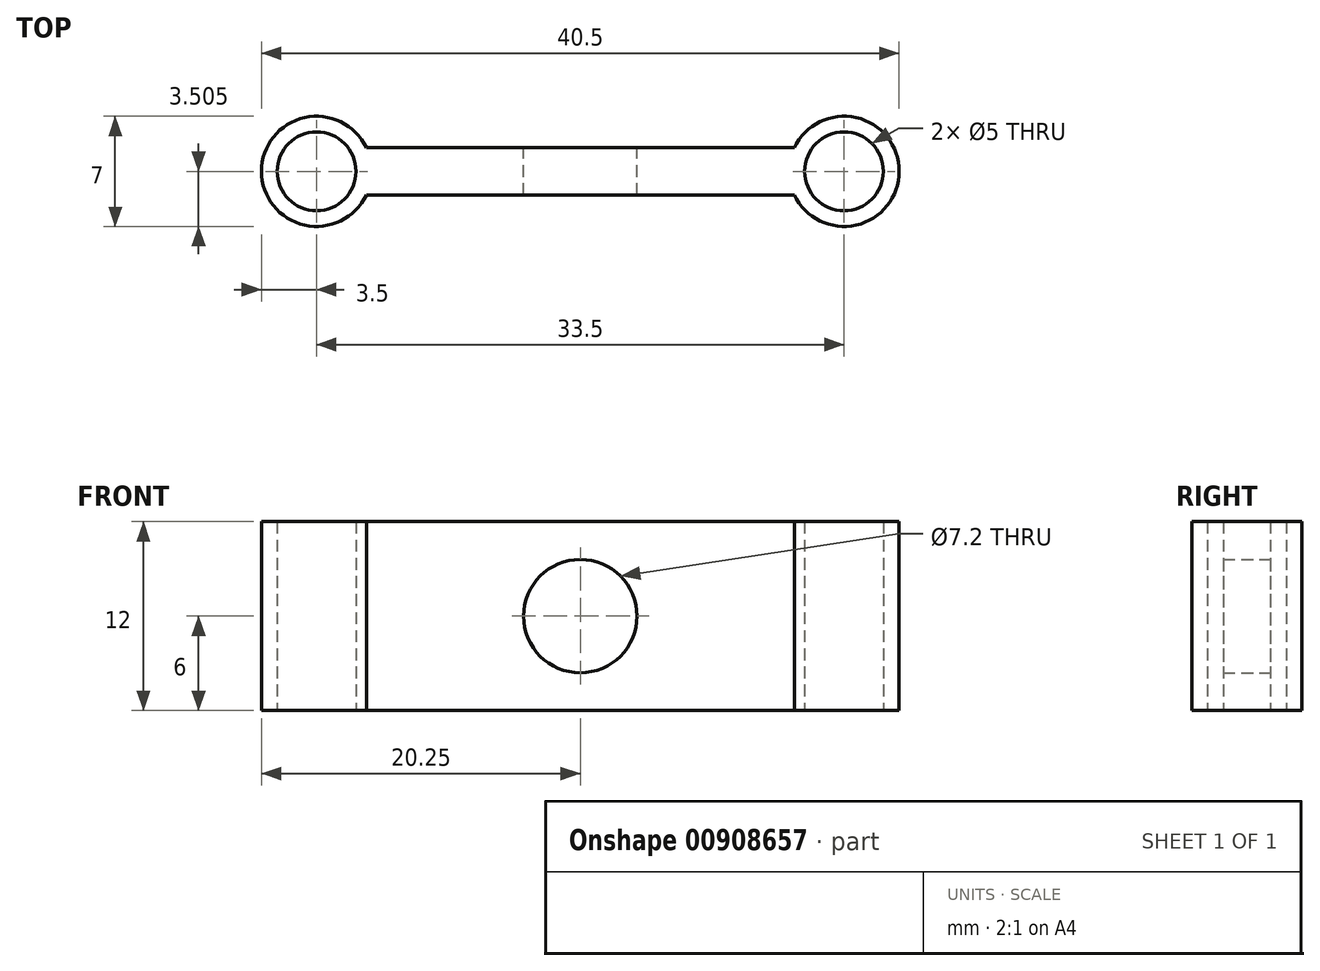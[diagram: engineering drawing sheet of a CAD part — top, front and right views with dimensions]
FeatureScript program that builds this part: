
annotation { "Feature Type Name" : "Feature", "Feature Type Description" : "" }
export const myFeature = defineFeature(function(context is Context, id is Id, definition is map)
    precondition{}
    {
        {
            var Q0;
            Q0=qCreatedBy(makeId("Top.planeOp"),FACE);
            var sketch = newSketch(context, id + "F0", { "sketchPlane" : qUnion([Q0])});
            skLineSegment(sketch, "E0.bottom", {"start": v(-14.5, 1.12) * mm, "end": v(19, 1.12) * mm});
            skLineSegment(sketch, "E0.top", {"start": v(-14.5, -1.88) * mm, "end": v(19, -1.88) * mm});
            skLineSegment(sketch, "E0.left", {"start": v(-14.5, 1.12) * mm, "end": v(-14.5, -1.88) * mm});
            skLineSegment(sketch, "E0.right", {"start": v(19, 1.12) * mm, "end": v(19, -1.88) * mm});
            skPoint(sketch, "E1", {"position": v(-14.5, -0.38) * mm});
            skCircle(sketch, "E2", {"center": v(-14.5, -0.38) * mm, "radius": 3.5 * mm});
            skCircle(sketch, "E3", {"center": v(19, -0.38) * mm, "radius": 3.5 * mm});
            skSolve(sketch);
        }
        {
            var Q0;
            Q0=qSketchRegion(id+"F0",true);
            extrude(context, id + "F1", {"entities" : qUnion([Q0]), "depth" : 12 * mm, "offsetDistance" : 25 * mm});
        }
        {
            var Q0;
            Q0=sQuery(id+"F0.wireOp",VERTEX,"35dba5de-8aa0-4c4d-8b60-120a7edc57c8");
            var Q1;
            Q1=sQuery(id+"F0.wireOp",VERTEX,"E3.center");
            var Q2;
            Q2=makeQuery(id+"F1.opExtrude","SWEPT_BODY",BODY,{"disambiguationData":[OSD([sQuery(id+"F0.wireOp",EDGE,"E0.bottom"),sQuery(id+"F0.wireOp",EDGE,"E0.top"),sQuery(id+"F0.wireOp",EDGE,"E2"),sQuery(id+"F0.wireOp",EDGE,"E3")])]});
            hole(context, id + "F2", {"style" : HoleStyle.SIMPLE, "endStyle" : HoleEndStyle.BLIND, "oppositeDirection" : true, "holeDiameter" : 5 * mm, "majorDiameter" : 5 * mm, "holeDepth" : 15 * mm, "isTappedThrough" : true, "tappedDepth" : 12 * mm, "tapClearance" : 3, "locations" : qUnion([Q0, Q1]), "scope" : qUnion([Q2])});
        }
        {
            var Q0;
            Q0=sQuery(id+"F0.wireOp",VERTEX,"E1");
            var Q1;
            Q1=makeQuery(id+"F1.opExtrude","SWEPT_BODY",BODY,{"disambiguationData":[OSD([sQuery(id+"F0.wireOp",EDGE,"E0.bottom"),sQuery(id+"F0.wireOp",EDGE,"E0.top"),sQuery(id+"F0.wireOp",EDGE,"E2"),sQuery(id+"F0.wireOp",EDGE,"E3")])]});
            hole(context, id + "F3", {"style" : HoleStyle.SIMPLE, "endStyle" : HoleEndStyle.BLIND, "oppositeDirection" : true, "holeDiameter" : 5 * mm, "majorDiameter" : 5 * mm, "holeDepth" : 15 * mm, "isTappedThrough" : true, "tappedDepth" : 12 * mm, "tapClearance" : 3, "locations" : qUnion([Q0]), "scope" : qUnion([Q1])});
        }
        {
            var Q0;
            Q0=makeQuery(id+"F1.opExtrude","SWEPT_FACE",FACE,{"disambiguationData":[OSD([sQuery(id+"F0.wireOp",EDGE,"E0.bottom")])]});
            var sketch = newSketch(context, id + "F4", { "sketchPlane" : qUnion([Q0])});
            skPoint(sketch, "E4", {"position": v(-2.25, 6) * mm});
            skPoint(sketch, "E4.positionSnap0", {"position": v(-2.25, 12) * mm});
            skPoint(sketch, "E5", {"position": v(-8.25, 6) * mm});
            skPoint(sketch, "E6", {"position": v(3.75, 6) * mm});
            skSolve(sketch);
        }
        {
            var Q0;
            Q0=sQuery(id+"F4.wireOp",VERTEX,"E4");
            var Q1;
            Q1=makeQuery(id+"F1.opExtrude","SWEPT_BODY",BODY,{"disambiguationData":[OSD([sQuery(id+"F0.wireOp",EDGE,"E0.bottom"),sQuery(id+"F0.wireOp",EDGE,"E0.top"),sQuery(id+"F0.wireOp",EDGE,"E2"),sQuery(id+"F0.wireOp",EDGE,"E3")])]});
            hole(context, id + "F5", {"style" : HoleStyle.SIMPLE, "endStyle" : HoleEndStyle.BLIND, "holeDiameter" : 7.2 * mm, "majorDiameter" : 5 * mm, "holeDepth" : 10 * mm, "isTappedThrough" : true, "tappedDepth" : 12 * mm, "tapClearance" : 3, "locations" : qUnion([Q0]), "scope" : qUnion([Q1])});
        }
    });
